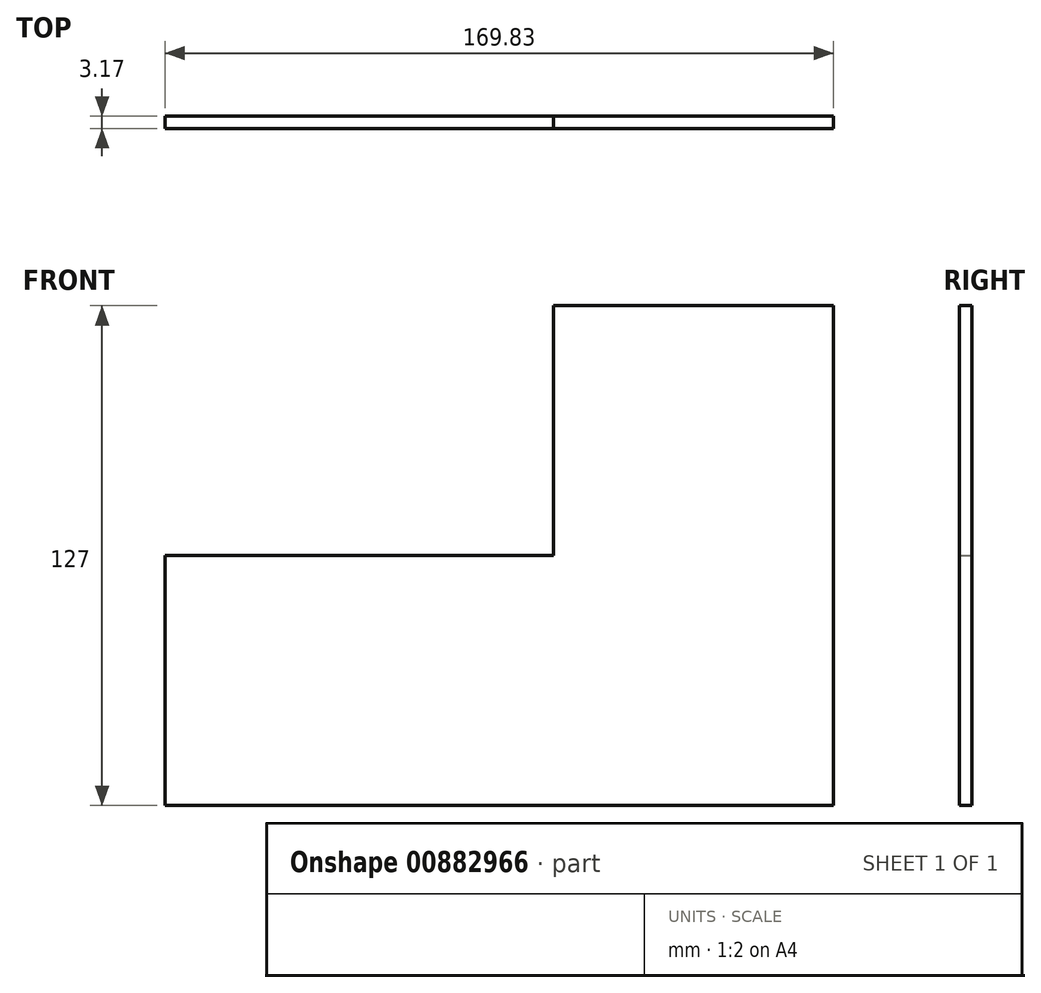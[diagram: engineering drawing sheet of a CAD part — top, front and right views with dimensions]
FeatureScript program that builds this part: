
annotation { "Feature Type Name" : "Feature", "Feature Type Description" : "" }
export const myFeature = defineFeature(function(context is Context, id is Id, definition is map)
    precondition{}
    {
        {
            var Q0;
            Q0=qCreatedBy(makeId("Front.planeOp"),FACE);
            var sketch = newSketch(context, id + "F0", { "sketchPlane" : qUnion([Q0])});
            skLineSegment(sketch, "E0", {"start": v(0, 0) * mm, "end": v(-98.7, 0) * mm});
            skLineSegment(sketch, "E1", {"start": v(-98.7, 0) * mm, "end": v(-98.7, -63.5) * mm});
            skLineSegment(sketch, "E2", {"start": v(-98.7, -63.5) * mm, "end": v(71.12, -63.5) * mm});
            skLineSegment(sketch, "E3", {"start": v(71.12, -63.5) * mm, "end": v(71.12, 63.5) * mm});
            skLineSegment(sketch, "E4", {"start": v(71.12, 63.5) * mm, "end": v(0, 63.5) * mm});
            skLineSegment(sketch, "E5", {"start": v(0, 63.5) * mm, "end": v(0, 0) * mm});
            skSolve(sketch);
        }
        {
            var Q0;
            Q0 = qSketchRegion(id + "F0", true);
            extrude(context, id + "F1", {"entities" : qUnion([Q0]), "depth" : 3.17 * mm, "offsetDistance" : 25.4 * mm});
        }
    });
